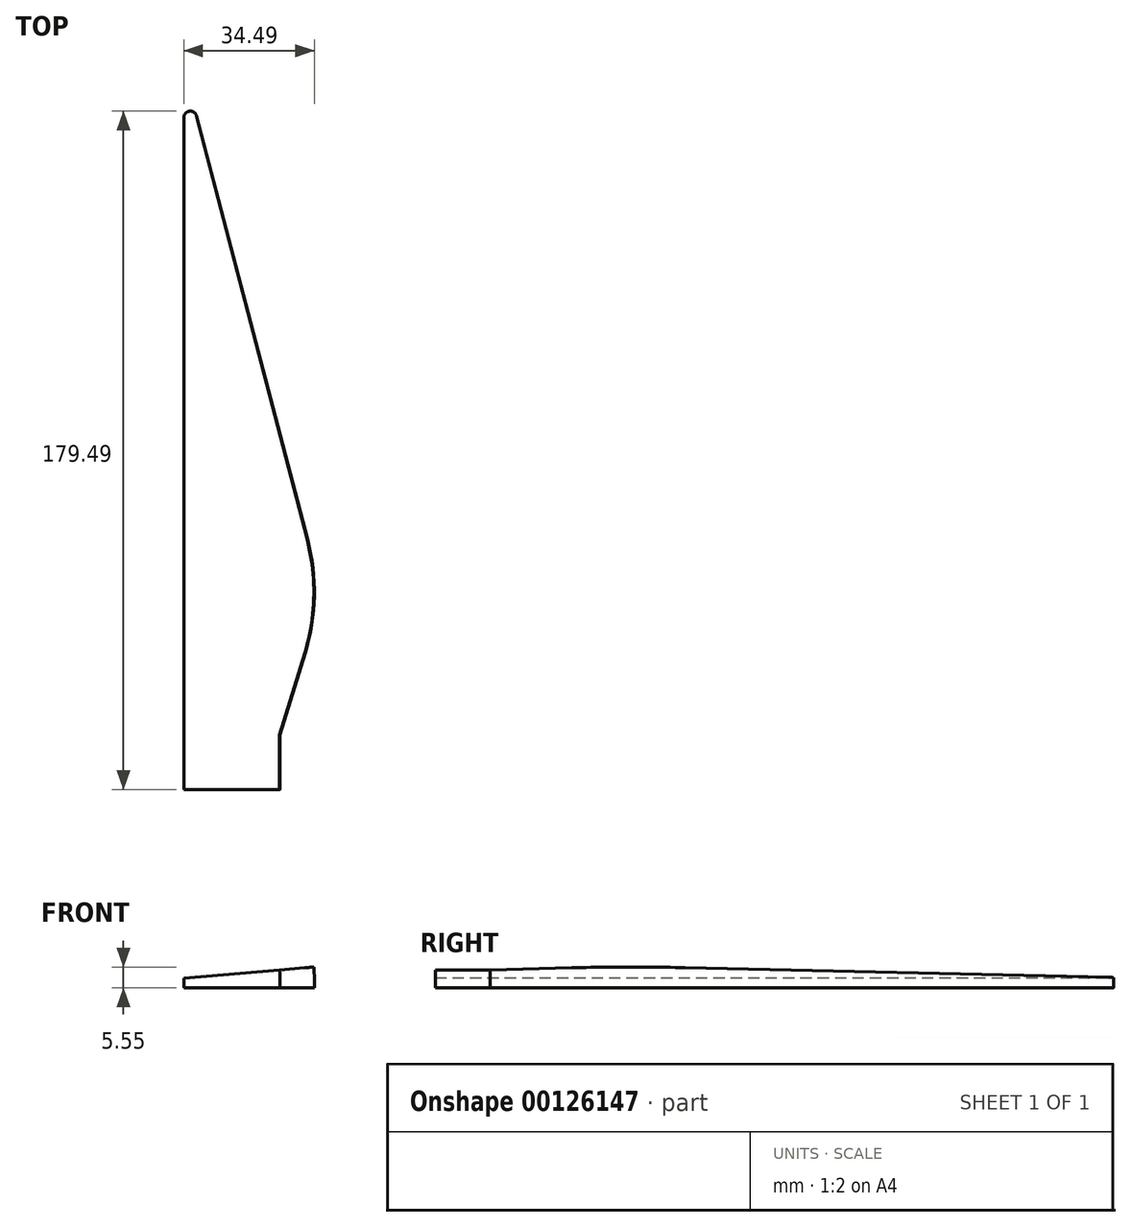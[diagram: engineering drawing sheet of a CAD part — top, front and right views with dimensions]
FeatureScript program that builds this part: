
annotation { "Feature Type Name" : "Feature", "Feature Type Description" : "" }
export const myFeature = defineFeature(function(context is Context, id is Id, definition is map)
    precondition{}
    {
        {
            var Q0;
            Q0=qCreatedBy(makeId("Top.planeOp"),FACE);
            var sketch = newSketch(context, id + "F0", { "sketchPlane" : qUnion([Q0])});
            skLineSegment(sketch, "E0", {"start": v(-72.71, 88.84) * mm, "end": v(-72.71, -88.96) * mm});
            skLineSegment(sketch, "E1", {"start": v(-72.71, -88.96) * mm, "end": v(-47.31, -88.96) * mm});
            skLineSegment(sketch, "E2", {"start": v(-47.31, -88.96) * mm, "end": v(-47.31, -74.48) * mm});
            skLineSegment(sketch, "E3", {"start": v(-47.31, -74.48) * mm, "end": v(-40.64, -52.8) * mm});
            skLineSegment(sketch, "E4", {"start": v(-40, -22.9) * mm, "end": v(-69.4, 89.27) * mm});
            skPoint(sketch, "E5.visualSharp", {"position": v(-36.06, -37.94) * mm});
            skArc(sketch, "E5.filletArc", {"start": v(-40.64, -52.8) * mm, "mid": v(-38.23, -37.9) * mm, "end": v(-40, -22.9) * mm});
            skPoint(sketch, "E6.visualSharp", {"position": v(-72.71, 101.95) * mm});
            skArc(sketch, "E6.filletArc", {"start": v(-69.4, 89.27) * mm, "mid": v(-71.24, 90.51) * mm, "end": v(-72.71, 88.84) * mm});
            skSolve(sketch);
        }
        {
            var Q0;
            Q0=makeQuery(id+"F0.imprint","IMPRINT",FACE,{"disambiguationData":[TD([[makeQuery(id+"F0.imprint","IMPRINT",EDGE,{"derivedFrom":sQuery(id+"F0.wireOp",EDGE,"E0")}),1.0]])]});
            extrude(context, id + "F1", {"entities" : qUnion([Q0]), "depth" : 2.54 * mm});
        }
        {
            var Q0;
            Q0=makeQuery(id+"F1.opExtrude","CAP_FACE",FACE,{"disambiguationData":[OSD([sQuery(id+"F0.wireOp",EDGE,"E0"),sQuery(id+"F0.wireOp",EDGE,"E1"),sQuery(id+"F0.wireOp",EDGE,"E2"),sQuery(id+"F0.wireOp",EDGE,"E3"),sQuery(id+"F0.wireOp",EDGE,"E4"),sQuery(id+"F0.wireOp",EDGE,"E5.filletArc"),sQuery(id+"F0.wireOp",EDGE,"E6.filletArc")])],"isStart":false});
            var Q1;
            Q1=makeQuery(id+"F1.opExtrude","CAP_EDGE",EDGE,{"disambiguationData":[OSD([sQuery(id+"F0.wireOp",EDGE,"E0")])],"isStart":false});
            revolve(context, id + "F2", {"operationType" : NewBodyOperationType.ADD, "entities" : qUnion([Q0]), "axis" : qUnion([Q1]), "revolveType" : RevolveType.ONE_DIRECTION, "angle" : 5 * degree});
        }
    });
